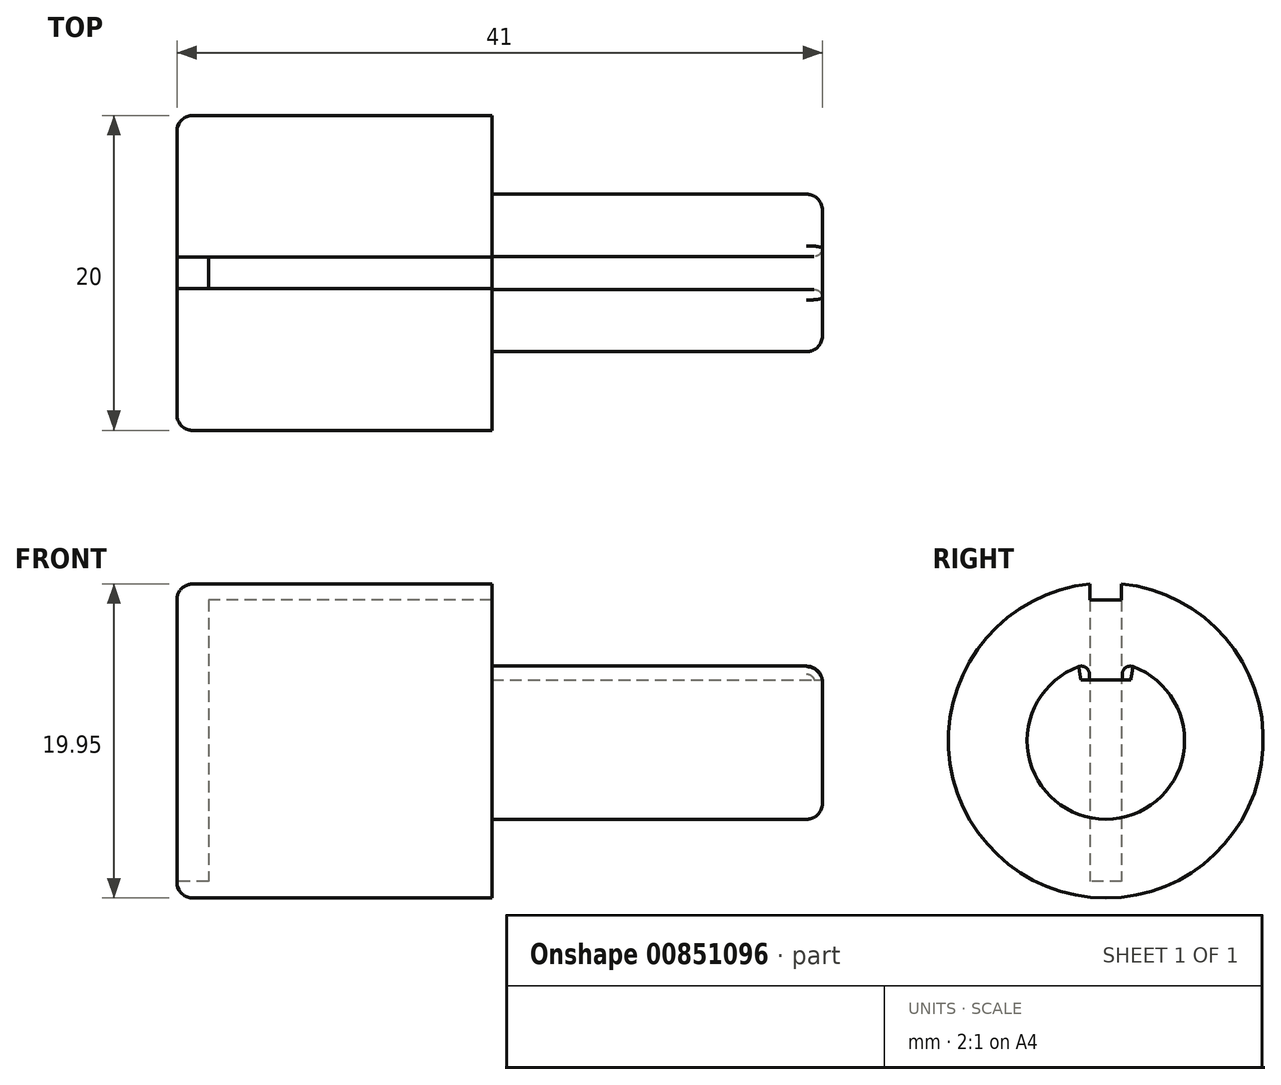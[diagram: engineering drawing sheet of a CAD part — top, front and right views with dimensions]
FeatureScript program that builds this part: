
annotation { "Feature Type Name" : "Feature", "Feature Type Description" : "" }
export const myFeature = defineFeature(function(context is Context, id is Id, definition is map)
    precondition{}
    {
        {
            var Q0;
            Q0=qCreatedBy(makeId("Top.planeOp"),FACE);
            var sketch = newSketch(context, id + "F0", { "sketchPlane" : qUnion([Q0])});
            skLineSegment(sketch, "E0.bottom", {"start": v(0, 0) * mm, "end": v(20, 0) * mm});
            skLineSegment(sketch, "E0.top", {"start": v(0, -10) * mm, "end": v(20, -10) * mm});
            skLineSegment(sketch, "E0.left", {"start": v(0, 0) * mm, "end": v(0, -10) * mm});
            skLineSegment(sketch, "E0.right", {"start": v(20, -5) * mm, "end": v(20, -10) * mm});
            skLineSegment(sketch, "E1.bottom", {"start": v(20, 0) * mm, "end": v(41, 0) * mm});
            skLineSegment(sketch, "E1.top", {"start": v(20, -5) * mm, "end": v(41, -5) * mm});
            skLineSegment(sketch, "E1.right", {"start": v(41, 0) * mm, "end": v(41, -5) * mm});
            skLineSegment(sketch, "E2", {"start": v(-25.98, 0) * mm, "end": v(58.02, 0) * mm, "construction": true});
            skSolve(sketch);
        }
        {
            var Q0;
            Q0 = qSketchRegion(id + "F0", true);
            var Q1;
            Q1=sQuery(id+"F0.wireOp",EDGE,"E2");
            revolve(context, id + "F1", {"surfaceOperationType" : NewSurfaceOperationType.NEW, "entities" : qUnion([Q0]), "axis" : qUnion([Q1]), "revolveType" : RevolveType.FULL});
        }
        {
            var Q0;
            Q0=makeQuery(id+"F1.opRevolve","SWEPT_EDGE",EDGE,{"disambiguationData":[OSD([sQuery(id+"F0.wireOp",EDGE,"E1.top"),sQuery(id+"F0.wireOp",EDGE,"E1.right")])]});
            var Q1;
            Q1=makeQuery(id+"F1.opRevolve","SWEPT_EDGE",EDGE,{"disambiguationData":[OSD([sQuery(id+"F0.wireOp",EDGE,"E0.top"),sQuery(id+"F0.wireOp",EDGE,"E0.left")])]});
            fillet(context, id + "F2", {"entities" : qUnion([Q0, Q1]), "radius" : 1 * mm, "tangentPropagation" : true, "allowEdgeOverflow" : false});
        }
        {
            var Q0;
            Q0=makeQuery(id+"F1.opRevolve","SWEPT_FACE",FACE,{"disambiguationData":[OSD([sQuery(id+"F0.wireOp",EDGE,"E0.left")])]});
            var sketch = newSketch(context, id + "F3", { "sketchPlane" : qUnion([Q0])});
            skLineSegment(sketch, "E3.bottom", {"start": v(-1, 8.94) * mm, "end": v(1, 8.94) * mm});
            skLineSegment(sketch, "E3.top", {"start": v(-1, -8.94) * mm, "end": v(1, -8.94) * mm});
            skLineSegment(sketch, "E3.left", {"start": v(-1, 8.94) * mm, "end": v(-1, -8.94) * mm});
            skLineSegment(sketch, "E3.right", {"start": v(1, 8.94) * mm, "end": v(1, -8.94) * mm});
            skSolve(sketch);
        }
        {
            var Q0;
            Q0 = qSketchRegion(id + "F3", true);
            extrude(context, id + "F4", {"entities" : qUnion([Q0]), "operationType" : NewBodyOperationType.REMOVE, "oppositeDirection" : true, "depth" : 2 * mm, "offsetDistance" : 25 * mm});
        }
        {
            var Q0;
            {var subQ0=sQuery(id+"F0.wireOp",EDGE,"E0.left");var subQ1=makeQuery(id+"F1.opRevolve","SWEPT_FACE",FACE,{"disambiguationData":[OSD([subQ0])]});Q0=makeQuery(id+"F4.boolean.opBoolean","SPLIT",FACE,{"disambiguationData":[TD([subQ1,makeQuery(id+"F2.opFillet","BLEND_FACE",FACE,{"disambiguationData":[OSD([sQuery(id+"F0.wireOp",EDGE,"E0.top"),subQ0])]}),makeQuery(id+"F4.opExtrude","SWEPT_FACE",FACE,{"disambiguationData":[OSD([sQuery(id+"F3.wireOp",EDGE,"E3.bottom")])]}),makeQuery(id+"F4.opExtrude","SWEPT_FACE",FACE,{"disambiguationData":[OSD([sQuery(id+"F3.wireOp",EDGE,"E3.top")])]}),makeQuery(id+"F4.opExtrude","SWEPT_FACE",FACE,{"disambiguationData":[OSD([sQuery(id+"F3.wireOp",EDGE,"E3.left")])]})])],"derivedFrom":subQ1});}
            var sketch = newSketch(context, id + "F5", { "sketchPlane" : qUnion([Q0])});
            skLineSegment(sketch, "E4.bottom", {"start": v(-1, 8.94) * mm, "end": v(1, 8.94) * mm});
            skLineSegment(sketch, "E4.top", {"start": v(-1, 10.41) * mm, "end": v(1, 10.41) * mm});
            skLineSegment(sketch, "E4.left", {"start": v(-1, 8.94) * mm, "end": v(-1, 10.41) * mm});
            skLineSegment(sketch, "E4.right", {"start": v(1, 8.94) * mm, "end": v(1, 10.41) * mm});
            skSolve(sketch);
        }
        {
            var Q0;
            Q0 = qSketchRegion(id + "F5", true);
            extrude(context, id + "F6", {"entities" : qUnion([Q0]), "operationType" : NewBodyOperationType.REMOVE, "endBound" : BoundingType.THROUGH_ALL, "oppositeDirection" : true, "depth" : 25 * mm, "offsetDistance" : 25 * mm});
        }
        {
            var Q0;
            Q0=makeQuery(id+"F1.opRevolve","SWEPT_FACE",FACE,{"disambiguationData":[OSD([sQuery(id+"F0.wireOp",EDGE,"E1.right")])]});
            var sketch = newSketch(context, id + "F7", { "sketchPlane" : qUnion([Q0])});
            skLineSegment(sketch, "E5.bottom", {"start": v(-1.05, 3.86) * mm, "end": v(1.05, 3.86) * mm});
            skLineSegment(sketch, "E5.top", {"start": v(-1.05, 5.13) * mm, "end": v(1.05, 5.13) * mm});
            skLineSegment(sketch, "E5.left", {"start": v(-1.05, 3.86) * mm, "end": v(-1.05, 5.13) * mm});
            skLineSegment(sketch, "E5.right", {"start": v(1.05, 3.86) * mm, "end": v(1.05, 5.13) * mm});
            skSolve(sketch);
        }
        {
            var Q0;
            Q0 = qSketchRegion(id + "F7", true);
            var Q1;
            Q1=makeQuery(id+"F1.opRevolve","SWEPT_FACE",FACE,{"disambiguationData":[OSD([sQuery(id+"F0.wireOp",EDGE,"E0.right")])]});
            extrude(context, id + "F8", {"entities" : qUnion([Q0]), "operationType" : NewBodyOperationType.REMOVE, "endBound" : BoundingType.UP_TO_SURFACE, "oppositeDirection" : true, "depth" : 25 * mm, "endBoundEntityFace" : qUnion([Q1]), "offsetDistance" : 25 * mm});
        }
        {
            var Q0;
            Q0=makeQuery(id+"F8.boolean.opBoolean","INTERSECT",EDGE,{"derivedFrom":[makeQuery(id+"F1.opRevolve","SWEPT_FACE",FACE,{"disambiguationData":[OSD([sQuery(id+"F0.wireOp",EDGE,"E1.top")])]}),makeQuery(id+"F8.opExtrude","SWEPT_FACE",FACE,{"disambiguationData":[OSD([sQuery(id+"F7.wireOp",EDGE,"E5.right")])]})]});
            var Q1;
            Q1=makeQuery(id+"F8.boolean.opBoolean","INTERSECT",EDGE,{"derivedFrom":[makeQuery(id+"F1.opRevolve","SWEPT_FACE",FACE,{"disambiguationData":[OSD([sQuery(id+"F0.wireOp",EDGE,"E1.top")])]}),makeQuery(id+"F8.opExtrude","SWEPT_FACE",FACE,{"disambiguationData":[OSD([sQuery(id+"F7.wireOp",EDGE,"E5.left")])]})]});
            fillet(context, id + "F9", {"entities" : qUnion([Q0, Q1]), "radius" : 0.5 * mm, "tangentPropagation" : true, "allowEdgeOverflow" : false});
        }
    });
